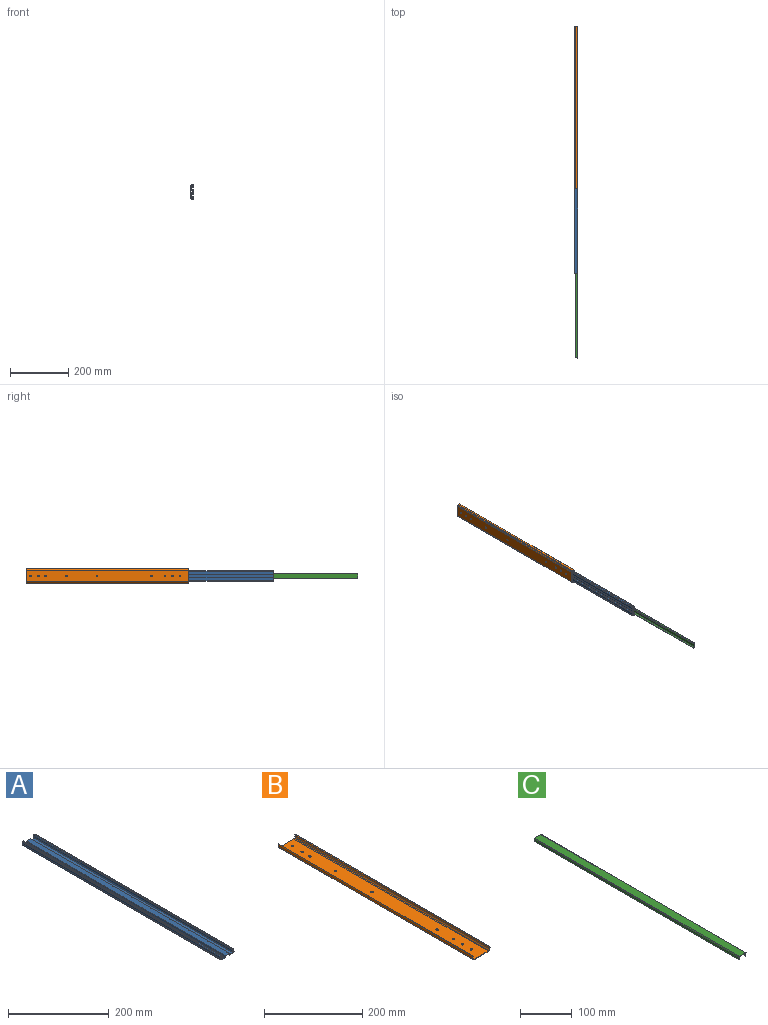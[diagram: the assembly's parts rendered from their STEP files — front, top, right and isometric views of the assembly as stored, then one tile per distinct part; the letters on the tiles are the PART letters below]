
ASSEMBLY  parts=3 mates=2
PART A: 34 faces, bbox 37.6x557.3x9.8 mm
  f0: plane 557.28x1.94mm, normal (0,0,1), area 1079.9mm2, adj f1,f31,f32,f33
  f1: cylinder r=1.19mm len=557.28mm, axis (0,-1,0), area 1374.5mm2, adj f0,f2,f32,f33
  f2: cylinder r=5.01mm len=557.28mm, axis (0,-1,0), area 2798.7mm2, adj f1,f3,f32,f33
  f3: cylinder r=2.15mm len=557.28mm, axis (0,-1,0), area 2477.6mm2, adj f2,f4,f32,f33
  f4: plane 557.28x11.1mm, normal (0,0,-1), area 6185.7mm2, adj f3,f5,f32,f33
  f5: plane 557.28x3.18mm, normal (0.97,0,-0.26), area 1831.8mm2, adj f4,f6,f32,f33
  f6: plane 557.28x9.41mm, normal (0,0,-1), area 5244.5mm2, adj f5,f7,f32,f33
  f7: plane 557.28x3.18mm, normal (-0.97,0,-0.26), area 1831.8mm2, adj f6,f8,f32,f33
  f8: plane 557.28x11.1mm, normal (0,0,-1), area 6185.7mm2, adj f7,f9,f32,f33
  f9: cylinder r=2.15mm len=557.28mm, axis (0,-1,0), area 2477.6mm2, adj f8,f10,f32,f33
  f10: cylinder r=5.01mm len=557.28mm, axis (0,-1,0), area 2798.7mm2, adj f9,f11,f32,f33
  f11: cylinder r=1.19mm len=557.28mm, axis (0,-1,0), area 1374.5mm2, adj f10,f12,f32,f33
  f12: plane 557.28x1.94mm, normal (0,0,1), area 1079.9mm2, adj f11,f13,f32,f33
  f13: cylinder r=1.19mm len=557.28mm, axis (0,-1,0), area 1314mm2, adj f12,f14,f32,f33
  f14: cylinder r=5.01mm len=557.28mm, axis (0,-1,0), area 3016.6mm2, adj f13,f15,f32,f33
  f15: plane 557.28x1.19mm, normal (-0.62,0,-0.78), area 849.3mm2, adj f14,f16,f32,f33
  f16: cylinder r=6.54mm len=557.28mm, axis (0,-1,0), area 3654.7mm2, adj f15,f17,f32,f33
  f17: plane 557.28x0.91mm, normal (0,0,-1), area 509.6mm2, adj f16,f18,f32,f33
  f18: cylinder r=6.54mm len=557.28mm, axis (0,-1,0), area 3342.6mm2, adj f17,f19,f32,f33
  f19: cylinder r=0.62mm len=557.28mm, axis (0,-1,0), area 718.1mm2, adj f18,f20,f32,f33
  f20: plane 557.28x9.93mm, normal (0,0,1), area 5534mm2, adj f19,f21,f32,f33
  f21: plane 557.28x3.18mm, normal (0.97,0,0.26), area 1831.8mm2, adj f20,f22,f32,f33
  f22: plane 557.28x11.75mm, normal (0,0,1), area 6547.9mm2, adj f21,f23,f32,f33
  f23: plane 557.28x3.18mm, normal (-0.97,0,0.26), area 1831.8mm2, adj f22,f24,f32,f33
  f24: plane 557.28x9.93mm, normal (0,0,1), area 5534mm2, adj f23,f25,f32,f33
  f25: cylinder r=0.62mm len=557.28mm, axis (0,-1,0), area 718.1mm2, adj f24,f26,f32,f33
  f26: cylinder r=6.54mm len=557.28mm, axis (0,-1,0), area 3342.6mm2, adj f25,f27,f32,f33
  f27: plane 557.28x0.91mm, normal (0,0,-1), area 509.6mm2, adj f26,f28,f32,f33
  f28: cylinder r=6.54mm len=557.28mm, axis (0,-1,0), area 3654.7mm2, adj f27,f29,f32,f33
  f29: plane 557.28x1.19mm, normal (0.62,0,-0.78), area 849.3mm2, adj f28,f30,f32,f33
  f30: cylinder r=5.01mm len=557.28mm, axis (0,-1,0), area 3016.6mm2, adj f29,f31,f32,f33
  f31: cylinder r=1.19mm len=557.28mm, axis (0,-1,0), area 1314mm2, adj f0,f30,f32,f33
  f32: plane 37.6x9.75mm, normal (0,1,0), area 114.5mm2, adj f0,f1,f2,f3,f4,f5,f6,f7
  f33: plane 37.6x9.75mm, normal (0,-1,0), area 114.5mm2, adj f0,f1,f2,f3,f4,f5,f6,f7
PART B: 54 faces, bbox 50.8x558.8x11.2 mm
  f0: plane 558.8x39.69mm, normal (0,0,1), area 22001.8mm2, adj f7,f8,f16,f17,f18,f19,f20,f21
  f1: plane 558.8x39.69mm, normal (0,0,-1), area 22001.8mm2, adj f14,f15,f16,f17,f18,f19,f20,f21
  f2: plane 558.8x2.71mm, normal (0.85,0,-0.52), area 1774.2mm2, adj f3,f15,f16,f17
  f3: cylinder r=6.54mm len=558.8mm, axis (0,-1,0), area 4006.2mm2, adj f2,f4,f16,f17
  f4: plane 558.8x1.3mm, normal (-0.52,0,0.85), area 851.6mm2, adj f3,f5,f16,f17
  f5: cylinder r=5.01mm len=558.8mm, axis (0,-1,0), area 3072.3mm2, adj f4,f6,f16,f17
  f6: plane 558.8x2.71mm, normal (-0.85,0,0.52), area 1774.2mm2, adj f5,f7,f16,f17
  f7: cylinder r=1.92mm len=558.8mm, axis (0,-1,0), area 1099.6mm2, adj f0,f6,f16,f17
  f8: cylinder r=1.92mm len=558.8mm, axis (0,-1,0), area 1099.6mm2, adj f0,f9,f16,f17
  f9: plane 558.8x2.71mm, normal (0.85,0,0.52), area 1774.2mm2, adj f8,f10,f16,f17
  f10: cylinder r=5.01mm len=558.8mm, axis (0,-1,0), area 3072.3mm2, adj f9,f11,f16,f17
  f11: plane 558.8x1.3mm, normal (0.52,0,0.85), area 851.6mm2, adj f10,f12,f16,f17
  f12: cylinder r=6.54mm len=558.8mm, axis (0,-1,0), area 4006.2mm2, adj f11,f13,f16,f17
  f13: plane 558.8x2.71mm, normal (-0.85,0,-0.52), area 1774.2mm2, adj f12,f14,f16,f17
  f14: cylinder r=3.45mm len=558.8mm, axis (0,-1,0), area 1970.4mm2, adj f1,f13,f16,f17
  f15: cylinder r=3.45mm len=558.8mm, axis (0,-1,0), area 1970.4mm2, adj f1,f2,f16,f17
  f16: plane 50.8x11.18mm, normal (0,1,0), area 97.8mm2, adj f0,f1,f2,f3,f4,f5,f6,f7
  f17: plane 50.8x11.18mm, normal (0,-1,0), area 97.8mm2, adj f0,f1,f2,f3,f4,f5,f6,f7
  f18: cylinder r=2.25mm len=4.5mm, axis (0,0,-1), area 10.8mm2, adj f0,f1,f19,f20
  f19: plane 1.52x0.8mm, normal (0,-1,0), area 1.2mm2, adj f0,f1,f18,f21
  f20: plane 1.52x0.8mm, normal (0,1,0), area 1.2mm2, adj f0,f1,f18,f21
  f21: cylinder r=2.25mm len=4.5mm, axis (0,0,-1), area 10.8mm2, adj f0,f1,f19,f20
  f22: cylinder r=2.25mm len=4.5mm, axis (0,0,-1), area 10.8mm2, adj f0,f1,f23,f24
  f23: plane 1.52x0.8mm, normal (0,-1,0), area 1.2mm2, adj f0,f1,f22,f25
  f24: plane 1.52x0.8mm, normal (0,1,0), area 1.2mm2, adj f0,f1,f22,f25
  f25: cylinder r=2.25mm len=4.5mm, axis (0,0,-1), area 10.8mm2, adj f0,f1,f23,f24
  f26: extruded ~4.5x2.25mm, area 10.8mm2, adj f0,f1,f27,f28
  f27: plane 1.52x0.8mm, normal (-1,0,0), area 1.2mm2, adj f0,f1,f26,f29
  f28: plane 1.52x0.8mm, normal (1,0,0), area 1.2mm2, adj f0,f1,f26,f29
  f29: extruded ~4.5x2.25mm, area 10.8mm2, adj f0,f1,f27,f28
  f30: extruded ~4.5x2.25mm, area 10.8mm2, adj f0,f1,f31,f32
  f31: plane 1.52x0.8mm, normal (1,0,0), area 1.2mm2, adj f0,f1,f30,f33
  f32: plane 1.52x0.8mm, normal (-1,0,0), area 1.2mm2, adj f0,f1,f30,f33
  f33: cylinder r=2.25mm len=4.5mm, axis (0,0,-1), area 10.8mm2, adj f0,f1,f31,f32
  f34: cylinder r=2.25mm len=4.5mm, axis (0,0,-1), area 10.8mm2, adj f0,f1,f35,f36
  f35: plane 1.52x0.8mm, normal (-1,0,0), area 1.2mm2, adj f0,f1,f34,f37
  f36: plane 1.52x0.8mm, normal (1,0,0), area 1.2mm2, adj f0,f1,f34,f37
  f37: cylinder r=2.25mm len=4.5mm, axis (0,0,-1), area 10.8mm2, adj f0,f1,f35,f36
  f38: extruded ~4.5x2.25mm, area 10.8mm2, adj f0,f1,f39,f40
  f39: plane 1.52x0.8mm, normal (1,0,0), area 1.2mm2, adj f0,f1,f38,f41
  f40: plane 1.52x0.8mm, normal (-1,0,0), area 1.2mm2, adj f0,f1,f38,f41
  f41: cylinder r=2.25mm len=4.5mm, axis (0,0,-1), area 10.8mm2, adj f0,f1,f39,f40
  f42: cylinder r=2.25mm len=4.5mm, axis (0,0,-1), area 10.8mm2, adj f0,f1,f43,f44
  f43: plane 1.52x0.8mm, normal (-1,0,0), area 1.2mm2, adj f0,f1,f42,f45
  f44: plane 1.52x0.8mm, normal (1,0,0), area 1.2mm2, adj f0,f1,f42,f45
  f45: extruded ~4.5x2.25mm, area 10.8mm2, adj f0,f1,f43,f44
  f46: extruded ~4.5x2.25mm, area 10.8mm2, adj f0,f1,f47,f48
  f47: plane 1.52x0.8mm, normal (1,0,0), area 1.2mm2, adj f0,f1,f46,f49
  f48: plane 1.52x0.8mm, normal (-1,0,0), area 1.2mm2, adj f0,f1,f46,f49
  f49: cylinder r=2.25mm len=4.5mm, axis (0,0,-1), area 10.8mm2, adj f0,f1,f47,f48
  f50: cylinder r=2.25mm len=4.5mm, axis (0,0,-1), area 10.8mm2, adj f0,f1,f51,f53
  f51: plane 1.52x0.8mm, normal (0,-1,0), area 1.2mm2, adj f0,f1,f50,f52
  f52: cylinder r=2.25mm len=4.5mm, axis (0,0,-1), area 10.8mm2, adj f0,f1,f51,f53
  f53: plane 1.52x0.8mm, normal (0,1,0), area 1.2mm2, adj f0,f1,f50,f52
PART C: 12 faces, bbox 19.7x557.3x7.8 mm
  f0: cylinder r=1.19mm len=557.28mm, axis (0,-1,0), area 1405.9mm2, adj f1,f9,f10,f11
  f1: plane 557.28x17.29mm, normal (0,0,1), area 9634.5mm2, adj f0,f2,f10,f11
  f2: cylinder r=1.19mm len=557.28mm, axis (0,-1,0), area 1405.9mm2, adj f1,f3,f10,f11
  f3: cylinder r=5.01mm len=557.28mm, axis (0,-1,0), area 3063mm2, adj f2,f4,f10,f11
  f4: plane 557.28x1.3mm, normal (-0.52,0,-0.85), area 849.3mm2, adj f3,f5,f10,f11
  f5: cylinder r=6.54mm len=557.28mm, axis (0,-1,0), area 3671.3mm2, adj f4,f6,f10,f11
  f6: plane 557.28x16.16mm, normal (0,0,-1), area 9005.8mm2, adj f5,f7,f10,f11
  f7: cylinder r=6.54mm len=557.28mm, axis (0,-1,0), area 3671.3mm2, adj f6,f8,f10,f11
  f8: plane 557.28x1.3mm, normal (0.52,0,-0.85), area 849.3mm2, adj f7,f9,f10,f11
  f9: cylinder r=5.01mm len=557.28mm, axis (0,-1,0), area 3063mm2, adj f0,f8,f10,f11
  f10: plane 19.67x7.83mm, normal (0,1,0), area 48.3mm2, adj f0,f1,f2,f3,f4,f5,f6,f7
  f11: plane 19.67x7.83mm, normal (0,-1,0), area 48.3mm2, adj f0,f1,f2,f3,f4,f5,f6,f7
PLACE A rot(axis=(0,1,0),90deg) t=(-949.02,-1092.57,-513.7)mm
PLACE B rot(axis=(0,1,0),90deg) t=(-949.02,-505.33,-513.69)mm fixed
PLACE C rot(axis=(0,1,0),90deg) t=(-949.01,-1676.77,-513.7)mm
MATE slider C.f11 <-> A.f33  axis (0,-1,0) through (-945.67,-1091.05,-522.06)mm
MATE slider A.f33 <-> B.f17  axis (0,-1,0) through (-948.36,-798.95,-530.36)mm
